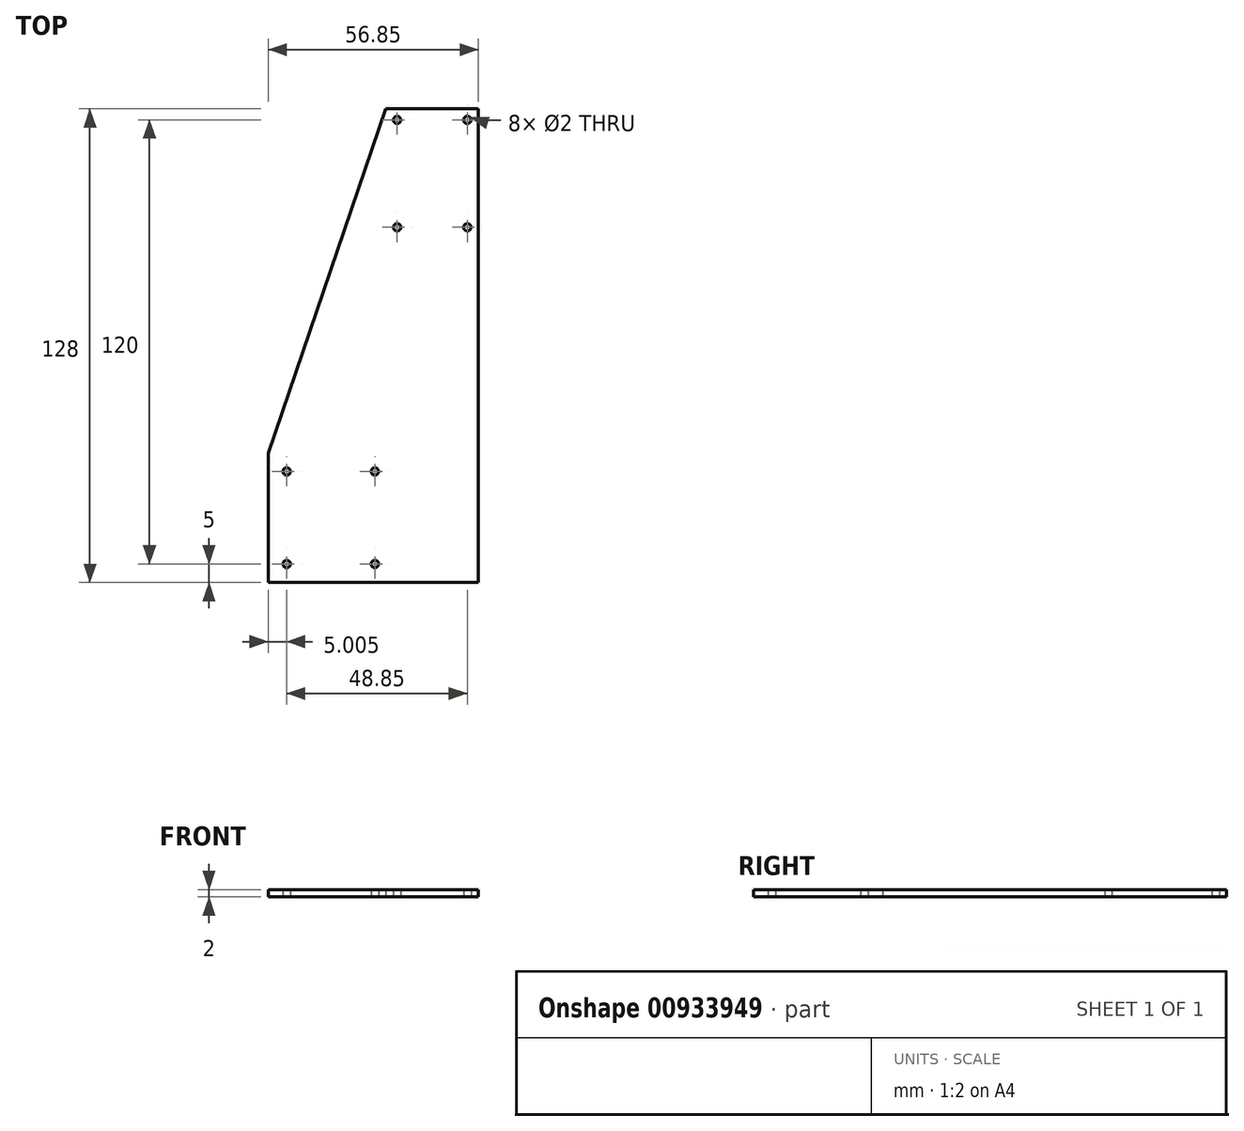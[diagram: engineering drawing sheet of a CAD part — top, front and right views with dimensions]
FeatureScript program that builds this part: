
annotation { "Feature Type Name" : "Feature", "Feature Type Description" : "" }
export const myFeature = defineFeature(function(context is Context, id is Id, definition is map)
    precondition{}
    {
        {
            var Q0;
            Q0=qCreatedBy(makeId("Top.planeOp"),FACE);
            var sketch = newSketch(context, id + "F0", { "sketchPlane" : qUnion([Q0])});
            skLineSegment(sketch, "E0.bottom", {"start": v(28.42, 64) * mm, "end": v(3.42, 64) * mm});
            skLineSegment(sketch, "E0.top", {"start": v(28.43, -64) * mm, "end": v(-28.42, -64) * mm});
            skLineSegment(sketch, "E0.left", {"start": v(28.42, 64) * mm, "end": v(28.43, -64) * mm});
            skLineSegment(sketch, "E0.right", {"start": v(-28.42, -29) * mm, "end": v(-28.42, -64) * mm});
            skPoint(sketch, "E0.middle", {"position": v(0, 0) * mm});
            skLineSegment(sketch, "E1.bottom", {"start": v(-23.42, -59) * mm, "end": v(0.43, -59) * mm, "construction": true});
            skLineSegment(sketch, "E1.top", {"start": v(-23.42, -34) * mm, "end": v(0.43, -34) * mm, "construction": true});
            skLineSegment(sketch, "E1.left", {"start": v(-23.42, -59) * mm, "end": v(-23.42, -34) * mm, "construction": true});
            skLineSegment(sketch, "E1.right", {"start": v(0.43, -59) * mm, "end": v(0.43, -34) * mm, "construction": true});
            skCircle(sketch, "E2", {"center": v(-23.42, -34) * mm, "radius": 1 * mm});
            skCircle(sketch, "E3", {"center": v(0.43, -34) * mm, "radius": 1 * mm});
            skCircle(sketch, "E4", {"center": v(0.43, -59) * mm, "radius": 1 * mm});
            skCircle(sketch, "E5", {"center": v(-23.42, -59) * mm, "radius": 1 * mm});
            skLineSegment(sketch, "E6", {"start": v(3.42, 64) * mm, "end": v(-28.42, -29) * mm});
            skPoint(sketch, "E7.orphan", {"position": v(-28.43, 64) * mm});
            skLineSegment(sketch, "E8.bottom", {"start": v(6.42, 61) * mm, "end": v(25.42, 61) * mm, "construction": true});
            skLineSegment(sketch, "E8.top", {"start": v(6.42, 32) * mm, "end": v(25.43, 32) * mm, "construction": true});
            skLineSegment(sketch, "E8.left", {"start": v(6.42, 61) * mm, "end": v(6.42, 32) * mm, "construction": true});
            skLineSegment(sketch, "E8.right", {"start": v(25.42, 61) * mm, "end": v(25.43, 32) * mm, "construction": true});
            skCircle(sketch, "E9", {"center": v(6.42, 61) * mm, "radius": 1 * mm});
            skCircle(sketch, "E10", {"center": v(25.42, 61) * mm, "radius": 1 * mm});
            skCircle(sketch, "E11", {"center": v(25.43, 32) * mm, "radius": 1 * mm});
            skCircle(sketch, "E12", {"center": v(6.42, 32) * mm, "radius": 1 * mm});
            skSolve(sketch);
        }
        {
            var Q0;
            Q0=makeQuery(id+"F0.imprint","IMPRINT",FACE,{"disambiguationData":[TD([[makeQuery(id+"F0.imprint","IMPRINT",EDGE,{"derivedFrom":sQuery(id+"F0.wireOp",EDGE,"E0.bottom")}),1.0]])]});
            extrude(context, id + "F1", {"entities" : qUnion([Q0]), "depth" : 2 * mm, "offsetDistance" : 25 * mm});
        }
    });
